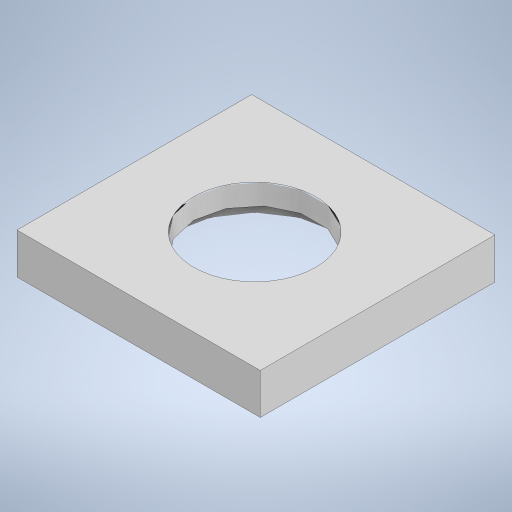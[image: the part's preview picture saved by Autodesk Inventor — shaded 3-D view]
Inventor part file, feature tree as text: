
AUTODESK INVENTOR PART (.ipt)
format: ipt  version: 2023 (Build 270158000, 158)  size: 632,832 bytes
history: native  units: in
note: dims shown in document units (in); Inventor stores cm internally (conversion verified against a paired STEP export)
features: extrude x16, sketch x14, fillet x2
ambient origin geometry x8: Origin, YZ Plane, XZ Plane, XY Plane, X Axis, Y Axis, Z Axis, Center Point
bodies: Solid1 (feature_tree)
feature tree (32):
  extrude  "Extrusion1"  Depth=4.5in
  extrude  "Extrusion2"  Depth=0.2in
  fillet  "Fillet1"  Radius=1.4in
  extrude  "Extrusion3"  Depth=0.25in
  extrude  "Extrusion4"  Depth=2.2875in
  extrude  "Extrusion5"  Depth=0.5437in
  sketch  "Sketch6"  dims[d13=0.75in d14=1.4in d15=0.0in]
  extrude  "Extrusion6"  Depth=1.4in TaperAngle=0.0deg
  extrude  "Extrusion9"  Depth=0.1in
  extrude  "Extrusion10"  Depth=0.1in
  extrude  "Extrusion11"  Depth=0.25in
  extrude  "Extrusion12"  Depth=0.15in
  extrude  "Extrusion13"  Depth=0.7in
  extrude  "Extrusion14"  Depth=0.1in
  extrude  "Extrusion15"  Depth=0.615in
  extrude  "Extrusion16"  Depth=0.2in
  fillet  "Fillet2"  Radius=0.21in
  extrude  "Extrusion17"  Depth=0.2in
  extrude  "Extrusion18"  Depth=0.2in
  sketch  "Sketch1"  dims[d0=7.0in d1=4.5in]
  sketch  "Sketch2"  dims[d2=1.5in d3=0.0in d4=0.2in d5=1.4in d6=0.0in]
  sketch  "Sketch3"  dims[d7=0.125in d8=0.25in]
  sketch  "Sketch4"  dims[d9=0.25in d10=2.2875in]
  sketch  "Sketch5"  dims[d11=3.4125in d12=0.5437in]
  sketch  "Sketch8"  dims[d16=0.1in d17=0.14in]
  sketch  "Sketch9"  dims[d18=0.1in d19=0.275in]
  sketch  "Sketch10"  dims[d20=0.35in d21=0.25in]
  sketch  "Sketch11"  dims[d22=0.15in d23=0.15in]
  sketch  "Sketch12"  dims[d24=0.25in d25=0.7in]
  sketch  "Sketch13"  dims[d26=0.1in d27=0.1in]
  sketch  "Sketch14"  dims[d28=0.25in d29=0.615in]
  sketch  "Sketch15"  dims[d30=0.25in d31=1.1in d32=0.21in d33=0.3075in d34=0.5575in d35=1.65in d36=0.3075in d37=0.21in d38=0.5575in d39=2.1in d40=0.1in d41=0.1in d42=0.3in d43=0.1in d44=0.25in d45=0.615in d46=2.4in d47=0.11in d48=2.51in d49=0.5575in d50=0.1in d51=0.615in d52=0.175in d53=0.175in d54=0.1in d55=0.1in d56=0.25in d57=3.15in d58=0.1in d59=0.515in d60=0.05in d61=0.0in d62=0.1562in d63=0.1562in d64=0.2188in d65=0.2188in d66=0.2188in d67=0.2188in d68=0.2188in d69=0.2188in d70=0.625in d71=0.625in d72=0.625in d73=0.625in d74=0.8906in d76=2.25in d77=0.3in d78=0.3in d79=0.3in d80=0.3in d81=0.3in d82=0.625in d83=0.625in d84=0.625in d85=0.625in d86=1.0in d87=3.1in d88=3.1in d89=3.1in d90=3.1in d91=3.1in d92=1.0in d93=0.0in d97=0.4in d98=0.4in d99=0.4in d100=0.4in d101=0.4in d102=0.05in d103=0.0in d119=0.075in d120=0.075in d121=0.075in d122=0.075in d123=0.075in d124=0.0688in d125=0.0in d126=0.25in d127=0.275in d128=0.25in d129=0.25in d130=0.25in d131=2.1in d132=0.125in d133=0.0625in d134=0.05in d135=0.0in d136=0.6in d137=3.35in d139=0.3in d140=0.3155in d141=0.3157in d142=0.0375in d143=0.0in d144=2.0in d145=0.8125in d146=0.0825in d147=0.35in d148=0.15in d149=0.1in d150=0.7in d151=0.2in d152=0.0in d153=0.075in d154=0.125in d155=0.0in d156=0.3in d157=2.5in d158=0.5in d159=0.25in d160=0.0in d161=0.5in d162=0.081in d163=0.0in d164=0.45in d165=0.6in d166=0.2in d167=0.2in d168=0.2in d169=0.075in d170=0.075in d171=0.075in d172=0.075in d173=0.2in d174=0.2in d175=0.2in d176=0.2in d177=0.075in d178=0.0in d179=0.125in d180=0.0375in d181=0.0375in d182=2.0in d183=0.5in d184=0.0in d185=0.0in d187=2.8in d188=5.0in d189=0.0in]
